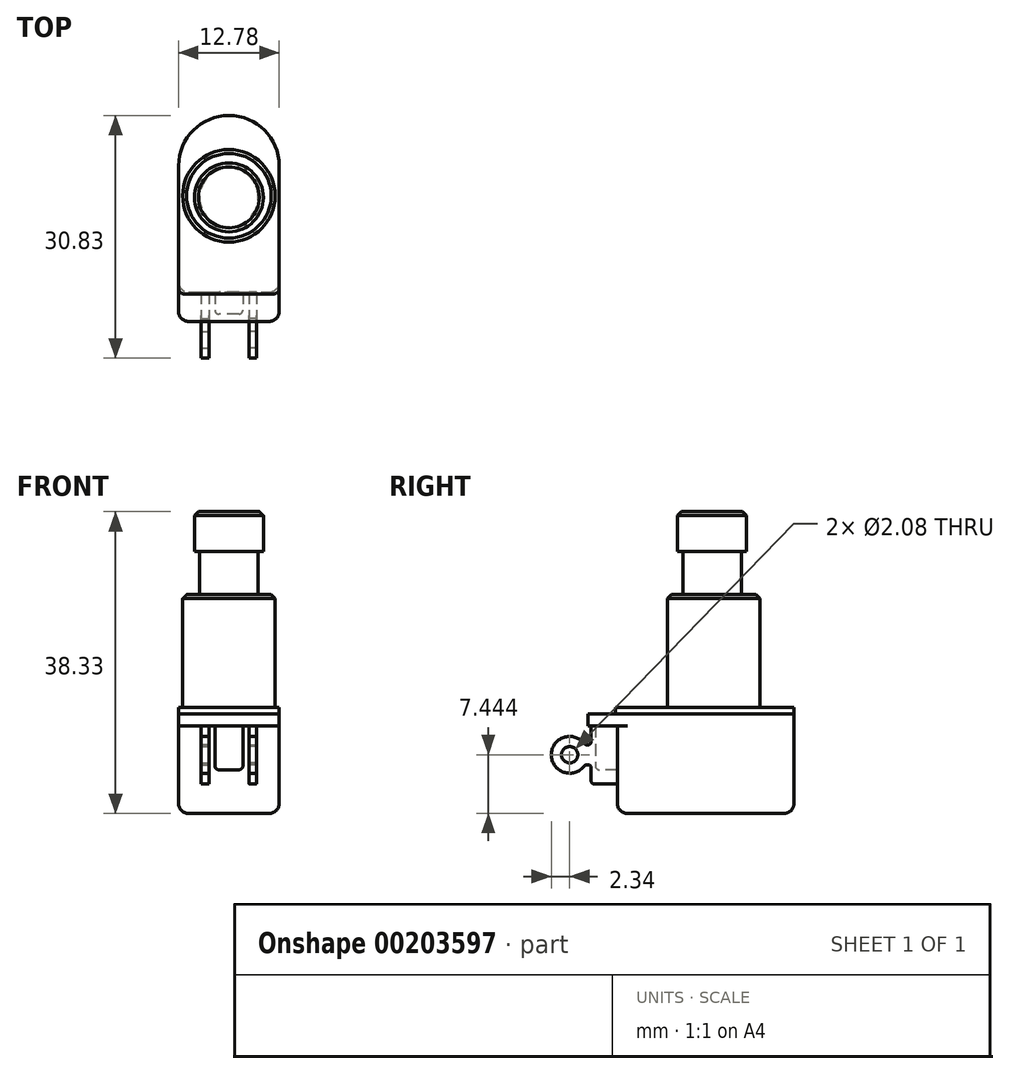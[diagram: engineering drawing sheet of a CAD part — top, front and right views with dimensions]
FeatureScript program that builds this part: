
annotation { "Feature Type Name" : "Feature", "Feature Type Description" : "" }
export const myFeature = defineFeature(function(context is Context, id is Id, definition is map)
    precondition{}
    {
        {
            var Q0;
            Q0=qCreatedBy(makeId("Top.planeOp"),FACE);
            var sketch = newSketch(context, id + "F0", { "sketchPlane" : qUnion([Q0])});
            skCircle(sketch, "E0", {"center": v(0, 0) * mm, "radius": 4.38 * mm});
            skSolve(sketch);
        }
        {
            var Q0;
            Q0 = qSketchRegion(id + "F0", true);
            extrude(context, id + "F1", {"entities" : qUnion([Q0]), "depth" : 5.08 * mm});
        }
        {
            var Q0;
            Q0=makeQuery(id+"F1.opExtrude","CAP_FACE",FACE,{"disambiguationData":[OSD([sQuery(id+"F0.wireOp",EDGE,"E0")])],"isStart":true});
            var sketch = newSketch(context, id + "F2", { "sketchPlane" : qUnion([Q0])});
            skCircle(sketch, "E1", {"center": v(0, 0) * mm, "radius": 3.72 * mm});
            skSolve(sketch);
        }
        {
            var Q0;
            Q0 = qSketchRegion(id + "F2", true);
            extrude(context, id + "F3", {"entities" : qUnion([Q0]), "operationType" : NewBodyOperationType.ADD, "depth" : 5.46 * mm});
        }
        {
            var Q0;
            Q0=makeQuery(id+"F3.opExtrude","CAP_FACE",FACE,{"disambiguationData":[OSD([sQuery(id+"F2.wireOp",EDGE,"E1")])],"isStart":false});
            var sketch = newSketch(context, id + "F4", { "sketchPlane" : qUnion([Q0])});
            skCircle(sketch, "E2", {"center": v(0, -0.2) * mm, "radius": 5.88 * mm});
            skSolve(sketch);
        }
        {
            var Q0;
            Q0 = qSketchRegion(id + "F4", true);
            extrude(context, id + "F5", {"entities" : qUnion([Q0]), "depth" : 14.3 * mm});
        }
        {
            var Q0;
            Q0=makeQuery(id+"F1.opExtrude","CAP_EDGE",EDGE,{"disambiguationData":[OSD([sQuery(id+"F0.wireOp",EDGE,"E0")])],"isStart":false});
            var Q1;
            Q1=makeQuery(id+"F5.opExtrude","CAP_EDGE",EDGE,{"disambiguationData":[OSD([sQuery(id+"F4.wireOp",EDGE,"E2")])],"isStart":true});
            chamfer(context, id + "F6", {"entities" : qUnion([Q0, Q1]), "width" : 0.5 * mm, "tangentPropagation" : true});
        }
        {
            var Q0;
            Q0=makeQuery(id+"F5.opExtrude","CAP_FACE",FACE,{"disambiguationData":[OSD([sQuery(id+"F4.wireOp",EDGE,"E2")])],"isStart":false});
            var sketch = newSketch(context, id + "F7", { "sketchPlane" : qUnion([Q0])});
            skLineSegment(sketch, "E3.bottom", {"start": v(-5.63, 12.28) * mm, "end": v(5.63, 12.28) * mm});
            skLineSegment(sketch, "E3.left", {"start": v(-6.39, 11.52) * mm, "end": v(-6.39, -4) * mm});
            skLineSegment(sketch, "E3.right", {"start": v(6.39, 11.52) * mm, "end": v(6.39, -4) * mm});
            skArc(sketch, "E4", {"start": v(-6.39, -4) * mm, "mid": v(0, -10.4) * mm, "end": v(6.39, -4) * mm});
            skPoint(sketch, "E5.visualSharp", {"position": v(-6.39, 12.28) * mm});
            skArc(sketch, "E5.filletArc", {"start": v(-5.63, 12.28) * mm, "mid": v(-6.16, 12.06) * mm, "end": v(-6.39, 11.52) * mm});
            skPoint(sketch, "E6.visualSharp", {"position": v(6.39, 12.28) * mm});
            skArc(sketch, "E6.filletArc", {"start": v(6.39, 11.52) * mm, "mid": v(6.16, 12.06) * mm, "end": v(5.63, 12.28) * mm});
            skSolve(sketch);
        }
        {
            var Q0;
            Q0 = qSketchRegion(id + "F7", true);
            extrude(context, id + "F8", {"entities" : qUnion([Q0]), "depth" : 0.86 * mm});
        }
        {
            var Q0;
            Q0=makeQuery(id+"F8.opExtrude","CAP_FACE",FACE,{"disambiguationData":[OSD([sQuery(id+"F7.wireOp",EDGE,"E3.bottom"),sQuery(id+"F7.wireOp",EDGE,"E3.left"),sQuery(id+"F7.wireOp",EDGE,"E3.right"),sQuery(id+"F7.wireOp",EDGE,"E4"),sQuery(id+"F7.wireOp",EDGE,"E5.filletArc"),sQuery(id+"F7.wireOp",EDGE,"E6.filletArc")])],"isStart":false});
            var sketch = newSketch(context, id + "F9", { "sketchPlane" : qUnion([Q0])});
            skArc(sketch, "E7.0", {"start": v(-6.39, -4) * mm, "mid": v(0, -10.4) * mm, "end": v(6.39, -4) * mm});
            skLineSegment(sketch, "E7.1", {"start": v(-6.39, 11.52) * mm, "end": v(-6.39, -4) * mm});
            skLineSegment(sketch, "E7.2", {"start": v(6.39, 11.52) * mm, "end": v(6.39, -4) * mm});
            skLineSegment(sketch, "E8", {"start": v(-6.39, 11.52) * mm, "end": v(-6.39, 14.5) * mm});
            skLineSegment(sketch, "E9", {"start": v(6.39, 11.52) * mm, "end": v(6.39, 14.5) * mm});
            skLineSegment(sketch, "E10", {"start": v(5.12, 15.76) * mm, "end": v(-5.12, 15.76) * mm});
            skPoint(sketch, "E11.visualSharp", {"position": v(-6.39, 15.76) * mm});
            skArc(sketch, "E11.filletArc", {"start": v(-5.12, 15.76) * mm, "mid": v(-6.02, 15.4) * mm, "end": v(-6.39, 14.5) * mm});
            skPoint(sketch, "E12.visualSharp", {"position": v(6.39, 15.76) * mm});
            skArc(sketch, "E12.filletArc", {"start": v(6.39, 14.5) * mm, "mid": v(6.02, 15.4) * mm, "end": v(5.12, 15.76) * mm});
            skSolve(sketch);
        }
        {
            var Q0;
            Q0 = qSketchRegion(id + "F9", true);
            extrude(context, id + "F10", {"entities" : qUnion([Q0]), "depth" : 1.5 * mm});
        }
        {
            var Q0;
            Q0=makeQuery(id+"F10.opExtrude","CAP_FACE",FACE,{"disambiguationData":[OSD([sQuery(id+"F9.wireOp",EDGE,"E7.0"),sQuery(id+"F9.wireOp",EDGE,"E7.1"),sQuery(id+"F9.wireOp",EDGE,"E7.2"),sQuery(id+"F9.wireOp",EDGE,"E8"),sQuery(id+"F9.wireOp",EDGE,"E9"),sQuery(id+"F9.wireOp",EDGE,"E10"),sQuery(id+"F9.wireOp",EDGE,"E11.filletArc"),sQuery(id+"F9.wireOp",EDGE,"E12.filletArc")])],"isStart":false});
            var sketch = newSketch(context, id + "F11", { "sketchPlane" : qUnion([Q0])});
            skArc(sketch, "E13.0", {"start": v(-6.39, -4) * mm, "mid": v(0, -10.4) * mm, "end": v(6.39, -4) * mm});
            skLineSegment(sketch, "E13.1", {"start": v(-6.39, 10.76) * mm, "end": v(-6.39, -4) * mm});
            skLineSegment(sketch, "E13.2", {"start": v(6.39, 10.76) * mm, "end": v(6.39, -4) * mm});
            skPoint(sketch, "E13.3", {"position": v(6.39, 3.76) * mm});
            skLineSegment(sketch, "E14", {"start": v(-5.12, 12.03) * mm, "end": v(5.12, 12.03) * mm});
            skPoint(sketch, "E15.visualSharp", {"position": v(-6.39, 12.03) * mm});
            skArc(sketch, "E15.filletArc", {"start": v(-5.12, 12.03) * mm, "mid": v(-6.02, 11.66) * mm, "end": v(-6.39, 10.76) * mm});
            skPoint(sketch, "E16.visualSharp", {"position": v(6.39, 12.03) * mm});
            skArc(sketch, "E16.filletArc", {"start": v(6.39, 10.76) * mm, "mid": v(6.02, 11.66) * mm, "end": v(5.12, 12.03) * mm});
            skSolve(sketch);
        }
        {
            var Q0;
            Q0 = qSketchRegion(id + "F11", true);
            extrude(context, id + "F12", {"entities" : qUnion([Q0]), "depth" : 11.13 * mm});
        }
        {
            var Q0;
            Q0=makeQuery(id+"F12.opExtrude","CAP_EDGE",EDGE,{"disambiguationData":[OSD([sQuery(id+"F11.wireOp",EDGE,"E13.1")])],"isStart":false});
            fillet(context, id + "F13", {"entities" : qUnion([Q0]), "radius" : 1.27 * mm, "tangentPropagation" : true, "allowEdgeOverflow" : false});
        }
        {
            var Q0;
            Q0=qCreatedBy(makeId("Right.planeOp"),FACE);
            var sketch = newSketch(context, id + "F14", { "sketchPlane" : qUnion([Q0])});
            skLineSegment(sketch, "E17.bottom", {"start": v(-12.03, -22.12) * mm, "end": v(-14.82, -22.12) * mm});
            skLineSegment(sketch, "E17.top", {"start": v(-12.03, -27.71) * mm, "end": v(-14.82, -27.71) * mm});
            skLineSegment(sketch, "E17.left", {"start": v(-12.03, -22.12) * mm, "end": v(-12.03, -27.71) * mm});
            skLineSegment(sketch, "E17.right", {"start": v(-14.82, -22.12) * mm, "end": v(-14.82, -27.71) * mm});
            skSolve(sketch);
        }
        {
            var Q0;
            Q0 = qSketchRegion(id + "F14", true);
            extrude(context, id + "F15", {"entities" : qUnion([Q0]), "operationType" : NewBodyOperationType.ADD, "depth" : 1.78 * mm, "hasSecondDirection" : true, "secondDirectionOppositeDirection" : true, "secondDirectionDepth" : 1.78 * mm});
        }
        {
            var Q0;
            Q0=makeQuery(id+"F15.opExtrude","SWEPT_EDGE",EDGE,{"disambiguationData":[OSD([sQuery(id+"F14.wireOp",EDGE,"E17.top"),sQuery(id+"F14.wireOp",EDGE,"E17.right")])]});
            var Q1;
            Q1=makeQuery(id+"F15.opExtrude","CAP_EDGE",EDGE,{"disambiguationData":[OSD([sQuery(id+"F14.wireOp",EDGE,"E17.right")])],"isStart":true});
            var Q2;
            Q2=makeQuery(id+"F15.opExtrude","CAP_EDGE",EDGE,{"disambiguationData":[OSD([sQuery(id+"F14.wireOp",EDGE,"E17.right")])],"isStart":false});
            var Q3;
            Q3=makeQuery(id+"F15.opExtrude","CAP_EDGE",EDGE,{"disambiguationData":[OSD([sQuery(id+"F14.wireOp",EDGE,"E17.top")])],"isStart":true});
            var Q4;
            Q4=makeQuery(id+"F15.opExtrude","CAP_EDGE",EDGE,{"disambiguationData":[OSD([sQuery(id+"F14.wireOp",EDGE,"E17.top")])],"isStart":false});
            fillet(context, id + "F16", {"entities" : qUnion([Q0, Q1, Q2, Q3, Q4]), "radius" : 0.5 * mm, "tangentPropagation" : true, "allowEdgeOverflow" : false});
        }
        {
            var Q0;
            Q0=qCreatedBy(makeId("Right.planeOp"),FACE);
            cPlane(context, id + "F17", {"entities" : qUnion([Q0]), "cplaneType" : CPlaneType.OFFSET, "offset" : 2.54 * mm, "width" : 152.4 * mm, "height" : 152.4 * mm});
        }
        {
            var Q0;
            Q0=qCreatedBy(id+"F17.planeOp",FACE);
            var sketch = newSketch(context, id + "F18", { "sketchPlane" : qUnion([Q0])});
            skLineSegment(sketch, "E18", {"start": v(-12.03, -22.12) * mm, "end": v(-15.38, -22.12) * mm});
            skLineSegment(sketch, "E19", {"start": v(-15.38, -22.12) * mm, "end": v(-15.38, -24.54) * mm});
            skLineSegment(sketch, "E20", {"start": v(-15.38, -24.54) * mm, "end": v(-16.13, -24.54) * mm});
            skLineSegment(sketch, "E21", {"start": v(-12.03, -22.12) * mm, "end": v(-12.03, -29.49) * mm});
            skLineSegment(sketch, "E22", {"start": v(-12.03, -29.49) * mm, "end": v(-15.37, -29.49) * mm});
            skLineSegment(sketch, "E23", {"start": v(-15.37, -29.49) * mm, "end": v(-15.37, -27.08) * mm});
            skLineSegment(sketch, "E24", {"start": v(-15.37, -27.08) * mm, "end": v(-16.13, -27.08) * mm});
            skArc(sketch, "E25", {"start": v(-16.13, -24.54) * mm, "mid": v(-20.43, -25.8) * mm, "end": v(-16.13, -27.08) * mm});
            skCircle(sketch, "E26", {"center": v(-18.1, -25.8) * mm, "radius": 1.04 * mm});
            skSolve(sketch);
        }
        {
            var Q0;
            Q0 = qSketchRegion(id + "F18", true);
            extrude(context, id + "F19", {"entities" : qUnion([Q0]), "depth" : 0.97 * mm});
        }
        {
            var Q0;
            Q0=makeQuery(id+"F19.opExtrude","SWEPT_BODY",BODY,{"disambiguationData":[OSD([sQuery(id+"F18.wireOp",EDGE,"E18"),sQuery(id+"F18.wireOp",EDGE,"E19"),sQuery(id+"F18.wireOp",EDGE,"E20"),sQuery(id+"F18.wireOp",EDGE,"E21"),sQuery(id+"F18.wireOp",EDGE,"E22"),sQuery(id+"F18.wireOp",EDGE,"E23"),sQuery(id+"F18.wireOp",EDGE,"E24"),sQuery(id+"F18.wireOp",EDGE,"E25"),sQuery(id+"F18.wireOp",EDGE,"E26")])]});
            var Q1;
            Q1=qCreatedBy(makeId("Right.planeOp"),FACE);
            mirror(context, id + "F20", {"entities" : qUnion([Q0]), "mirrorPlane" : qUnion([Q1])});
        }
        {
            var Q0;
            Q0=makeQuery(id+"F19.opExtrude","SWEPT_EDGE",EDGE,{"disambiguationData":[OSD([sQuery(id+"F18.wireOp",EDGE,"E22"),sQuery(id+"F18.wireOp",EDGE,"E23")])]});
            var Q1;
            Q1=makeQuery(id+"F20.opPattern","COPY",EDGE,{"derivedFrom":makeQuery(id+"F19.opExtrude","SWEPT_EDGE",EDGE,{"disambiguationData":[OSD([sQuery(id+"F18.wireOp",EDGE,"E22"),sQuery(id+"F18.wireOp",EDGE,"E23")])]}),"instanceName":"1"});
            var Q2;
            Q2=makeQuery(id+"F20.opPattern","COPY",EDGE,{"derivedFrom":makeQuery(id+"F19.opExtrude","SWEPT_EDGE",EDGE,{"disambiguationData":[OSD([sQuery(id+"F18.wireOp",EDGE,"E23"),sQuery(id+"F18.wireOp",EDGE,"E24")])]}),"instanceName":"1"});
            var Q3;
            Q3=makeQuery(id+"F19.opExtrude","SWEPT_EDGE",EDGE,{"disambiguationData":[OSD([sQuery(id+"F18.wireOp",EDGE,"E23"),sQuery(id+"F18.wireOp",EDGE,"E24")])]});
            var Q4;
            Q4=makeQuery(id+"F19.opExtrude","SWEPT_EDGE",EDGE,{"disambiguationData":[OSD([sQuery(id+"F18.wireOp",EDGE,"E24"),sQuery(id+"F18.wireOp",EDGE,"E25")])]});
            var Q5;
            Q5=makeQuery(id+"F20.opPattern","COPY",EDGE,{"derivedFrom":makeQuery(id+"F19.opExtrude","SWEPT_EDGE",EDGE,{"disambiguationData":[OSD([sQuery(id+"F18.wireOp",EDGE,"E24"),sQuery(id+"F18.wireOp",EDGE,"E25")])]}),"instanceName":"1"});
            var Q6;
            Q6=makeQuery(id+"F19.opExtrude","SWEPT_EDGE",EDGE,{"disambiguationData":[OSD([sQuery(id+"F18.wireOp",EDGE,"E19"),sQuery(id+"F18.wireOp",EDGE,"E20")])]});
            var Q7;
            Q7=makeQuery(id+"F19.opExtrude","SWEPT_EDGE",EDGE,{"disambiguationData":[OSD([sQuery(id+"F18.wireOp",EDGE,"E20"),sQuery(id+"F18.wireOp",EDGE,"E25")])]});
            var Q8;
            Q8=makeQuery(id+"F19.opExtrude","SWEPT_EDGE",EDGE,{"disambiguationData":[OSD([sQuery(id+"F18.wireOp",EDGE,"E18"),sQuery(id+"F18.wireOp",EDGE,"E19")])]});
            var Q9;
            Q9=makeQuery(id+"F20.opPattern","COPY",EDGE,{"derivedFrom":makeQuery(id+"F19.opExtrude","SWEPT_EDGE",EDGE,{"disambiguationData":[OSD([sQuery(id+"F18.wireOp",EDGE,"E18"),sQuery(id+"F18.wireOp",EDGE,"E19")])]}),"instanceName":"1"});
            var Q10;
            Q10=makeQuery(id+"F20.opPattern","COPY",EDGE,{"derivedFrom":makeQuery(id+"F19.opExtrude","SWEPT_EDGE",EDGE,{"disambiguationData":[OSD([sQuery(id+"F18.wireOp",EDGE,"E19"),sQuery(id+"F18.wireOp",EDGE,"E20")])]}),"instanceName":"1"});
            var Q11;
            Q11=makeQuery(id+"F20.opPattern","COPY",EDGE,{"derivedFrom":makeQuery(id+"F19.opExtrude","SWEPT_EDGE",EDGE,{"disambiguationData":[OSD([sQuery(id+"F18.wireOp",EDGE,"E20"),sQuery(id+"F18.wireOp",EDGE,"E25")])]}),"instanceName":"1"});
            fillet(context, id + "F21", {"entities" : qUnion([Q0, Q1, Q2, Q3, Q4, Q5, Q6, Q7, Q8, Q9, Q10, Q11]), "radius" : 0.38 * mm, "tangentPropagation" : true, "allowEdgeOverflow" : false});
        }
    });
